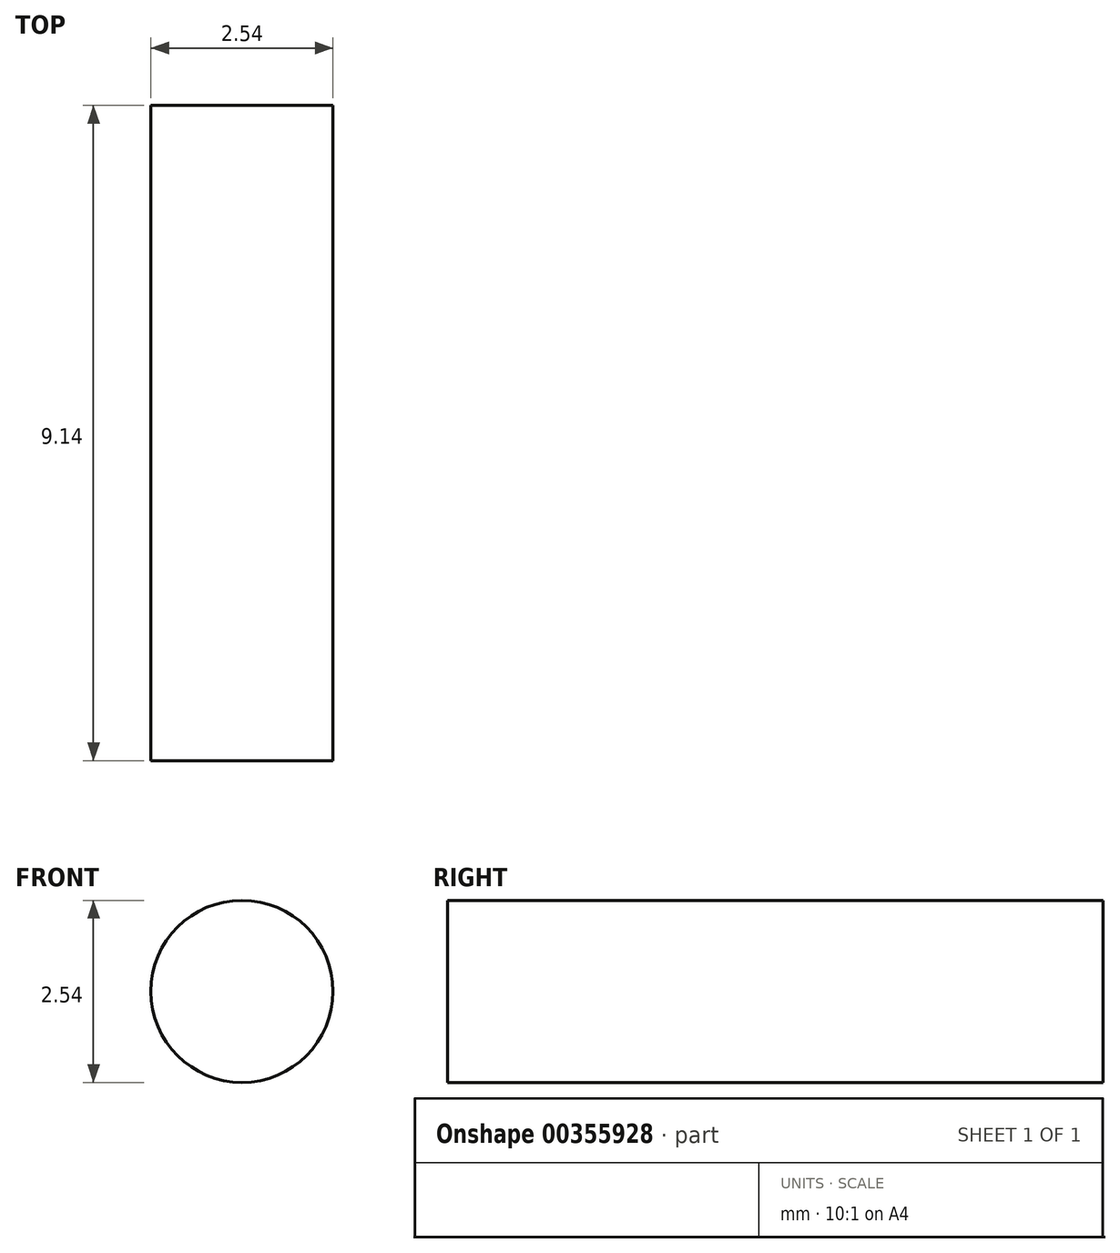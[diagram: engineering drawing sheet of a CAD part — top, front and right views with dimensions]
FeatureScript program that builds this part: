
annotation { "Feature Type Name" : "Feature", "Feature Type Description" : "" }
export const myFeature = defineFeature(function(context is Context, id is Id, definition is map)
    precondition{}
    {
        {
            var Q0;
            Q0=qCreatedBy(makeId("Front.planeOp"),FACE);
            var sketch = newSketch(context, id + "F0", { "sketchPlane" : qUnion([Q0])});
            skCircle(sketch, "E0", {"center": v(0, 0) * mm, "radius": 1.27 * mm});
            skSolve(sketch);
        }
        {
            var Q0;
            Q0=qSketchRegion(id+"F0",true);
            extrude(context, id + "F1", {"entities" : qUnion([Q0]), "depth" : 9.14 * mm});
        }
    });
